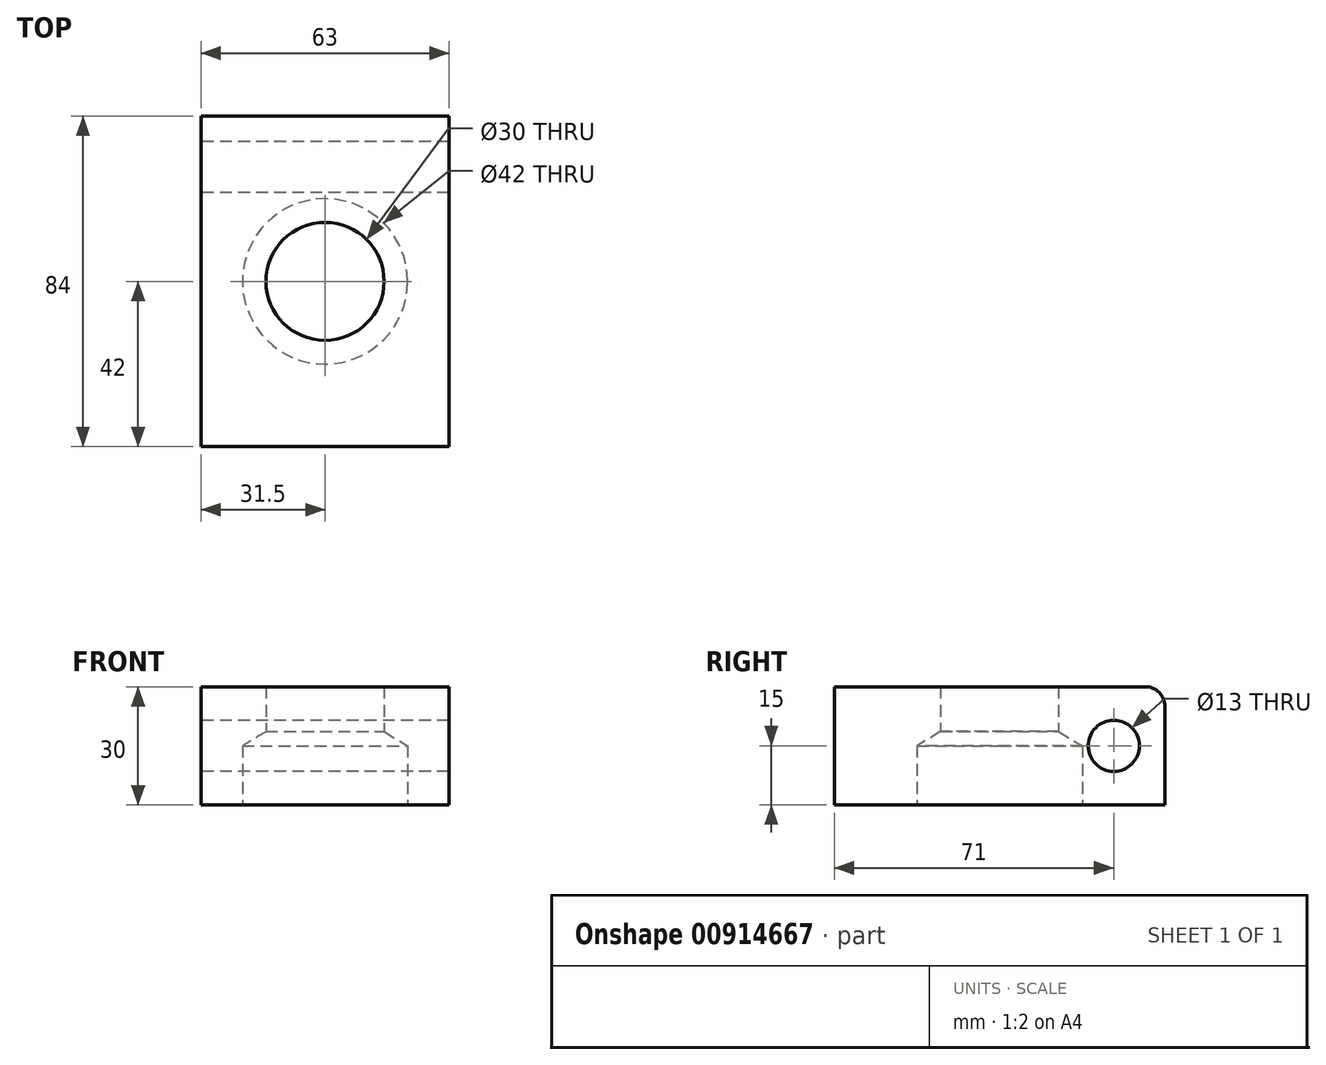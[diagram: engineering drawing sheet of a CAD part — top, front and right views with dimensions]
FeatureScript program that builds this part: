
annotation { "Feature Type Name" : "Feature", "Feature Type Description" : "" }
export const myFeature = defineFeature(function(context is Context, id is Id, definition is map)
    precondition{}
    {
        {
            var Q0;
            Q0=qCreatedBy(makeId("Top.planeOp"),FACE);
            var sketch = newSketch(context, id + "F0", { "sketchPlane" : qUnion([Q0])});
            skLineSegment(sketch, "E0.bottom", {"start": v(31.5, -42) * mm, "end": v(-31.5, -42) * mm});
            skLineSegment(sketch, "E0.top", {"start": v(31.5, 42) * mm, "end": v(-31.5, 42) * mm});
            skLineSegment(sketch, "E0.left", {"start": v(31.5, -42) * mm, "end": v(31.5, 42) * mm});
            skLineSegment(sketch, "E0.right", {"start": v(-31.5, -42) * mm, "end": v(-31.5, 42) * mm});
            skPoint(sketch, "E0.middle", {"position": v(0, 0) * mm});
            skPoint(sketch, "E1", {"position": v(0, 42) * mm});
            skSolve(sketch);
        }
        {
            var Q0;
            Q0=qCreatedBy(makeId("Top.planeOp"),FACE);
            var sketch = newSketch(context, id + "F1", { "sketchPlane" : qUnion([Q0])});
            skCircle(sketch, "E2", {"center": v(0, 0) * mm, "radius": 15 * mm});
            skSolve(sketch);
        }
        {
            var Q0;
            Q0=makeQuery(id+"F0.imprint","IMPRINT",FACE,{"disambiguationData":[TD([[makeQuery(id+"F0.imprint","IMPRINT",EDGE,{"derivedFrom":sQuery(id+"F0.wireOp",EDGE,"E0.bottom")}),-1.0]])]});
            extrude(context, id + "F2", {"entities" : qUnion([Q0]), "depth" : 30 * mm, "offsetDistance" : 25 * mm});
        }
        {
            var Q0;
            Q0=sQuery(id+"F1.wireOp",VERTEX,"E2.center");
            var Q1;
            Q1=makeQuery(id+"F2.opExtrude","SWEPT_BODY",BODY,{"disambiguationData":[OSD([sQuery(id+"F0.wireOp",EDGE,"E0.bottom"),sQuery(id+"F0.wireOp",EDGE,"E0.top"),sQuery(id+"F0.wireOp",EDGE,"E0.left"),sQuery(id+"F0.wireOp",EDGE,"E0.right")])]});
            hole(context, id + "F3", {"style" : HoleStyle.SIMPLE, "endStyle" : HoleEndStyle.THROUGH, "oppositeDirection" : true, "holeDiameter" : 30 * mm, "majorDiameter" : 5 * mm, "isTappedThrough" : true, "tappedDepth" : 12 * mm, "tapClearance" : 3, "locations" : qUnion([Q0]), "scope" : qUnion([Q1])});
        }
        {
            var Q0;
            Q0=qCreatedBy(makeId("Top.planeOp"),FACE);
            var sketch = newSketch(context, id + "F4", { "sketchPlane" : qUnion([Q0])});
            skPoint(sketch, "E3", {"position": v(0, 0) * mm});
            skSolve(sketch);
        }
        {
            var Q0;
            Q0=sQuery(id+"F4.wireOp",VERTEX,"E3");
            var Q1;
            Q1=makeQuery(id+"F2.opExtrude","SWEPT_BODY",BODY,{"disambiguationData":[OSD([sQuery(id+"F0.wireOp",EDGE,"E0.bottom"),sQuery(id+"F0.wireOp",EDGE,"E0.top"),sQuery(id+"F0.wireOp",EDGE,"E0.left"),sQuery(id+"F0.wireOp",EDGE,"E0.right")])]});
            hole(context, id + "F5", {"style" : HoleStyle.SIMPLE, "endStyle" : HoleEndStyle.BLIND, "oppositeDirection" : true, "holeDiameter" : 42 * mm, "majorDiameter" : 5 * mm, "holeDepth" : 15 * mm, "isTappedThrough" : true, "tappedDepth" : 12 * mm, "tapClearance" : 3, "locations" : qUnion([Q0]), "scope" : qUnion([Q1])});
        }
        {
            var Q0;
            Q0=makeQuery(id+"F2.opExtrude","SWEPT_FACE",FACE,{"disambiguationData":[OSD([sQuery(id+"F0.wireOp",EDGE,"E0.right")])]});
            var sketch = newSketch(context, id + "F6", { "sketchPlane" : qUnion([Q0])});
            skLineSegment(sketch, "E4", {"start": v(-42, 15) * mm, "end": v(-29, 15) * mm});
            skLineSegment(sketch, "E5", {"start": v(-29, 15) * mm, "end": v(-29, 0) * mm});
            skPoint(sketch, "E6", {"position": v(-29, 15) * mm});
            skSolve(sketch);
        }
        {
            var Q0;
            Q0=sQuery(id+"F6.wireOp",VERTEX,"E6");
            var Q1;
            Q1=makeQuery(id+"F2.opExtrude","SWEPT_BODY",BODY,{"disambiguationData":[OSD([sQuery(id+"F0.wireOp",EDGE,"E0.bottom"),sQuery(id+"F0.wireOp",EDGE,"E0.top"),sQuery(id+"F0.wireOp",EDGE,"E0.left"),sQuery(id+"F0.wireOp",EDGE,"E0.right")])]});
            hole(context, id + "F7", {"style" : HoleStyle.SIMPLE, "endStyle" : HoleEndStyle.THROUGH, "holeDiameter" : 13 * mm, "majorDiameter" : 5 * mm, "isTappedThrough" : true, "tappedDepth" : 12 * mm, "tapClearance" : 3, "locations" : qUnion([Q0]), "scope" : qUnion([Q1])});
        }
        {
            var Q0;
            Q0=makeQuery(id+"F2.opExtrude","CAP_EDGE",EDGE,{"disambiguationData":[OSD([sQuery(id+"F0.wireOp",EDGE,"E0.top")])],"isStart":false});
            fillet(context, id + "F8", {"entities" : qUnion([Q0]), "radius" : 5 * mm, "tangentPropagation" : true, "allowEdgeOverflow" : false});
        }
    });
